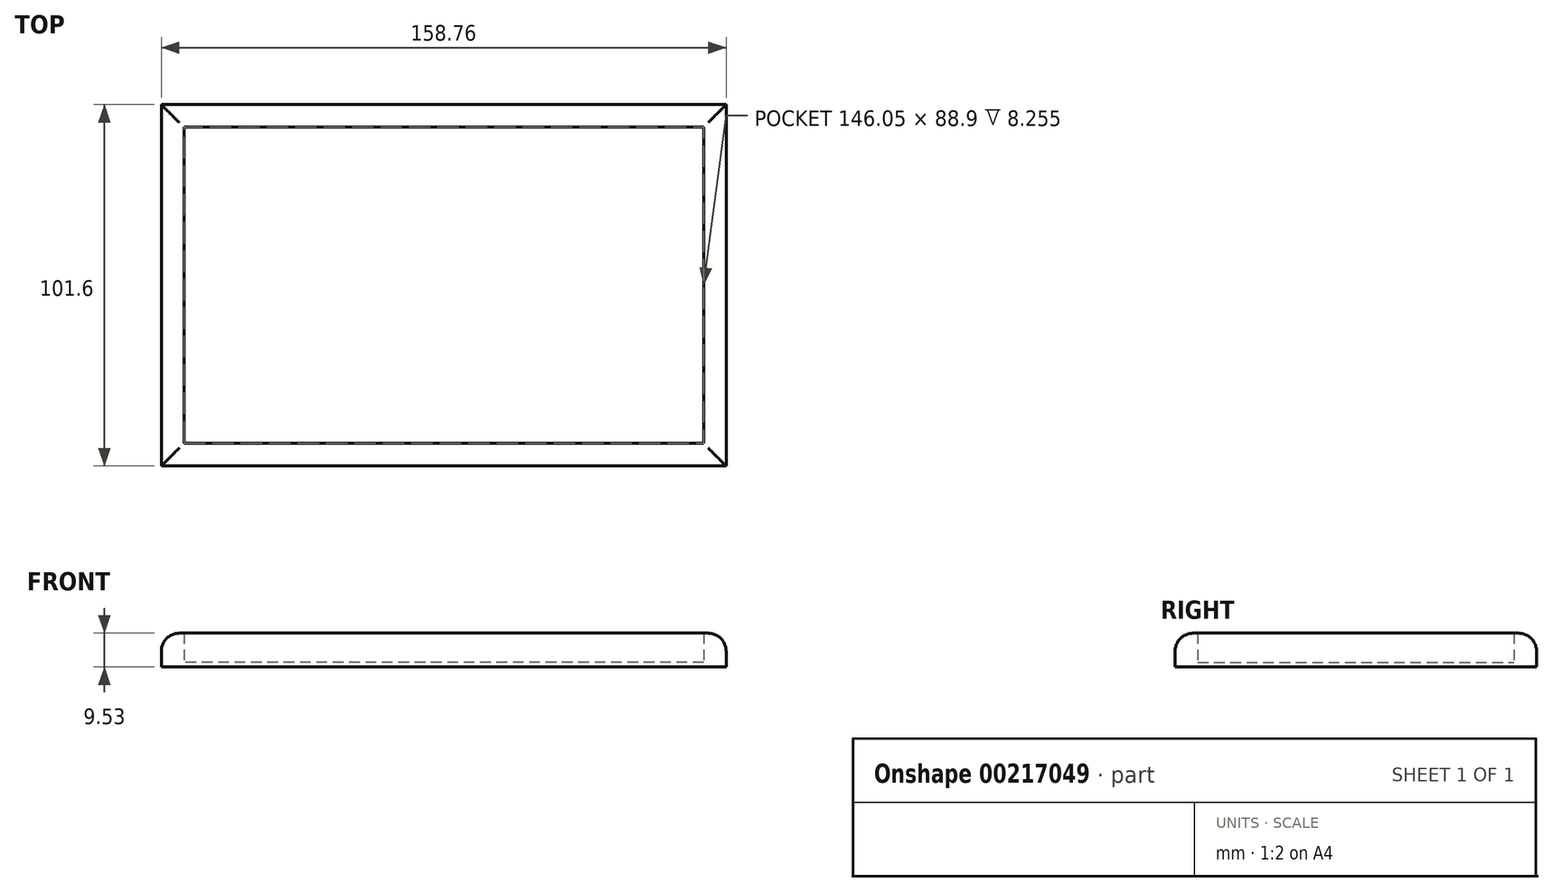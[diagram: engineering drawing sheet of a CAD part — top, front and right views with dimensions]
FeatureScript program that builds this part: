
annotation { "Feature Type Name" : "Feature", "Feature Type Description" : "" }
export const myFeature = defineFeature(function(context is Context, id is Id, definition is map)
    precondition{}
    {
        {
            var Q0;
            Q0=qCreatedBy(makeId("Top.planeOp"),FACE);
            var sketch = newSketch(context, id + "F0", { "sketchPlane" : qUnion([Q0])});
            skPoint(sketch, "E0.middle", {"position": v(0, 0) * mm});
            skLineSegment(sketch, "E1.0", {"start": v(79.38, 50.8) * mm, "end": v(-79.38, 50.8) * mm});
            skLineSegment(sketch, "E1.1", {"start": v(79.38, -50.8) * mm, "end": v(79.38, 50.8) * mm});
            skLineSegment(sketch, "E1.2", {"start": v(79.38, -50.8) * mm, "end": v(-79.38, -50.8) * mm});
            skLineSegment(sketch, "E1.3", {"start": v(-79.38, -50.8) * mm, "end": v(-79.38, 50.8) * mm});
            skLineSegment(sketch, "E2.0", {"start": v(-73.03, -44.45) * mm, "end": v(-73.03, 44.45) * mm});
            skLineSegment(sketch, "E2.1", {"start": v(73.03, -44.45) * mm, "end": v(-73.03, -44.45) * mm});
            skLineSegment(sketch, "E2.2", {"start": v(73.03, -44.45) * mm, "end": v(73.03, 44.45) * mm});
            skLineSegment(sketch, "E2.3", {"start": v(73.03, 44.45) * mm, "end": v(-73.03, 44.45) * mm});
            skPoint(sketch, "E0.right.end.orphan", {"position": v(-76.2, 47.62) * mm});
            skPoint(sketch, "E0.bottom.end.orphan", {"position": v(-76.2, -47.63) * mm});
            skPoint(sketch, "E0.left.end.orphan", {"position": v(76.2, 47.63) * mm});
            skPoint(sketch, "E0.left.start.orphan", {"position": v(76.2, -47.62) * mm});
            skSolve(sketch);
        }
        {
            var Q0;
            Q0 = qSketchRegion(id + "F0", true);
            extrude(context, id + "F1", {"entities" : qUnion([Q0]), "depth" : 9.52 * mm});
        }
        {
            var Q0;
            Q0=makeQuery(id+"F1.opExtrude","CAP_EDGE",EDGE,{"disambiguationData":[OSD([sQuery(id+"F0.wireOp",EDGE,"E1.3")])],"isStart":false});
            var Q1;
            Q1=makeQuery(id+"F1.opExtrude","CAP_EDGE",EDGE,{"disambiguationData":[OSD([sQuery(id+"F0.wireOp",EDGE,"E1.2")])],"isStart":false});
            var Q2;
            Q2=makeQuery(id+"F1.opExtrude","CAP_EDGE",EDGE,{"disambiguationData":[OSD([sQuery(id+"F0.wireOp",EDGE,"E1.1")])],"isStart":false});
            var Q3;
            Q3=makeQuery(id+"F1.opExtrude","CAP_EDGE",EDGE,{"disambiguationData":[OSD([sQuery(id+"F0.wireOp",EDGE,"E1.0")])],"isStart":false});
            fillet(context, id + "F2", {"entities" : qUnion([Q0, Q1, Q2, Q3]), "radius" : 5.08 * mm, "tangentPropagation" : true, "allowEdgeOverflow" : false});
        }
        {
            var Q0;
            Q0=makeQuery(id+"F0.imprint","IMPRINT",FACE,{"disambiguationData":[TD([[makeQuery(id+"F0.imprint","IMPRINT",EDGE,{"derivedFrom":sQuery(id+"F0.wireOp",EDGE,"E2.0")}),-1.0]])]});
            extrude(context, id + "F3", {"entities" : qUnion([Q0]), "operationType" : NewBodyOperationType.ADD, "depth" : 1.27 * mm});
        }
    });
